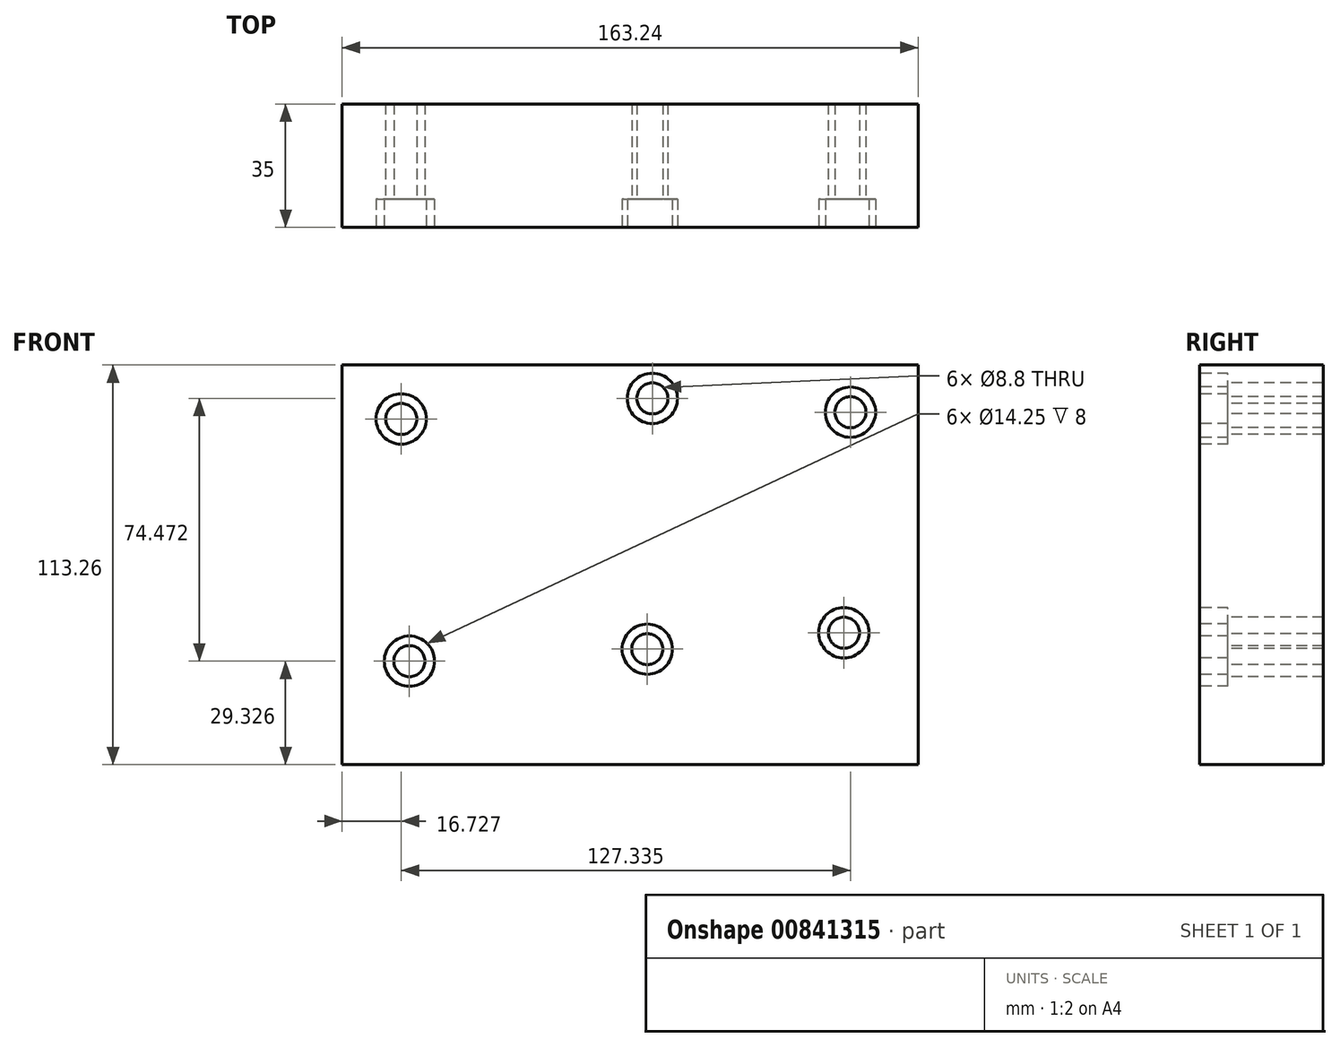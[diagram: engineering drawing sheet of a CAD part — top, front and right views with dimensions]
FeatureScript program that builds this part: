
annotation { "Feature Type Name" : "Feature", "Feature Type Description" : "" }
export const myFeature = defineFeature(function(context is Context, id is Id, definition is map)
    precondition{}
    {
        {
            var Q0;
            Q0=qCreatedBy(makeId("Front.planeOp"),FACE);
            var sketch = newSketch(context, id + "F0", { "sketchPlane" : qUnion([Q0])});
            skLineSegment(sketch, "E0.bottom", {"start": v(81.62, -56.63) * mm, "end": v(-81.62, -56.63) * mm});
            skLineSegment(sketch, "E0.top", {"start": v(81.62, 56.63) * mm, "end": v(-81.62, 56.63) * mm});
            skLineSegment(sketch, "E0.left", {"start": v(81.62, -56.63) * mm, "end": v(81.62, 56.63) * mm});
            skLineSegment(sketch, "E0.right", {"start": v(-81.62, -56.63) * mm, "end": v(-81.62, 56.63) * mm});
            skPoint(sketch, "E0.middle", {"position": v(0, 0) * mm});
            skSolve(sketch);
        }
        {
            var Q0;
            Q0 = qSketchRegion(id + "F0", true);
            extrude(context, id + "F1", {"entities" : qUnion([Q0]), "oppositeDirection" : true, "depth" : 35 * mm, "offsetDistance" : 25 * mm});
        }
        {
            var Q0;
            Q0=makeQuery(id+"F1.opExtrude","CAP_FACE",FACE,{"disambiguationData":[OSD([sQuery(id+"F0.wireOp",EDGE,"E0.bottom"),sQuery(id+"F0.wireOp",EDGE,"E0.top"),sQuery(id+"F0.wireOp",EDGE,"E0.left"),sQuery(id+"F0.wireOp",EDGE,"E0.right")])],"isStart":true});
            var sketch = newSketch(context, id + "F2", { "sketchPlane" : qUnion([Q0])});
            skPoint(sketch, "E1", {"position": v(-64.9, 41.34) * mm});
            skPoint(sketch, "E2", {"position": v(62.44, 43.26) * mm});
            skPoint(sketch, "E3", {"position": v(60.58, -19.27) * mm});
            skPoint(sketch, "E4", {"position": v(-62.58, -27.3) * mm});
            skPoint(sketch, "E5", {"position": v(6.3, 47.17) * mm});
            skPoint(sketch, "E6", {"position": v(4.85, -23.9) * mm});
            skSolve(sketch);
        }
        {
            var Q0;
            Q0=sQuery(id+"F2.wireOp",VERTEX,"E1");
            var Q1;
            Q1=sQuery(id+"F2.wireOp",VERTEX,"E5");
            var Q2;
            Q2=sQuery(id+"F2.wireOp",VERTEX,"E2");
            var Q3;
            Q3=sQuery(id+"F2.wireOp",VERTEX,"E3");
            var Q4;
            Q4=sQuery(id+"F2.wireOp",VERTEX,"E6");
            var Q5;
            Q5=sQuery(id+"F2.wireOp",VERTEX,"E4");
            var Q6;
            Q6=makeQuery(id+"F1.opExtrude","SWEPT_BODY",BODY,{"disambiguationData":[OSD([sQuery(id+"F0.wireOp",EDGE,"E0.bottom"),sQuery(id+"F0.wireOp",EDGE,"E0.top"),sQuery(id+"F0.wireOp",EDGE,"E0.left"),sQuery(id+"F0.wireOp",EDGE,"E0.right")])]});
            hole(context, id + "F3", {"style" : HoleStyle.C_BORE, "endStyle" : HoleEndStyle.THROUGH, "standardTappedOrClearance" : lookupTablePath({ "fit" : "Normal", "standard" : "ISO", "size" : "M8", "type" : "Clearance" }), "standardBlindInLast" : lookupTablePath({ "fit" : "Standard", "standard" : "ISO", "size" : "M8", "type" : "Clearance" }), "holeDiameter" : 8.8 * mm, "cBoreDiameter" : 14.25 * mm, "cBoreDepth" : 8 * mm, "majorDiameter" : 5 * mm, "isTappedThrough" : true, "tappedDepth" : 12 * mm, "tapClearance" : 3, "startFromSketch" : true, "locations" : qUnion([Q0, Q1, Q2, Q3, Q4, Q5]), "scope" : qUnion([Q6])});
        }
    });
